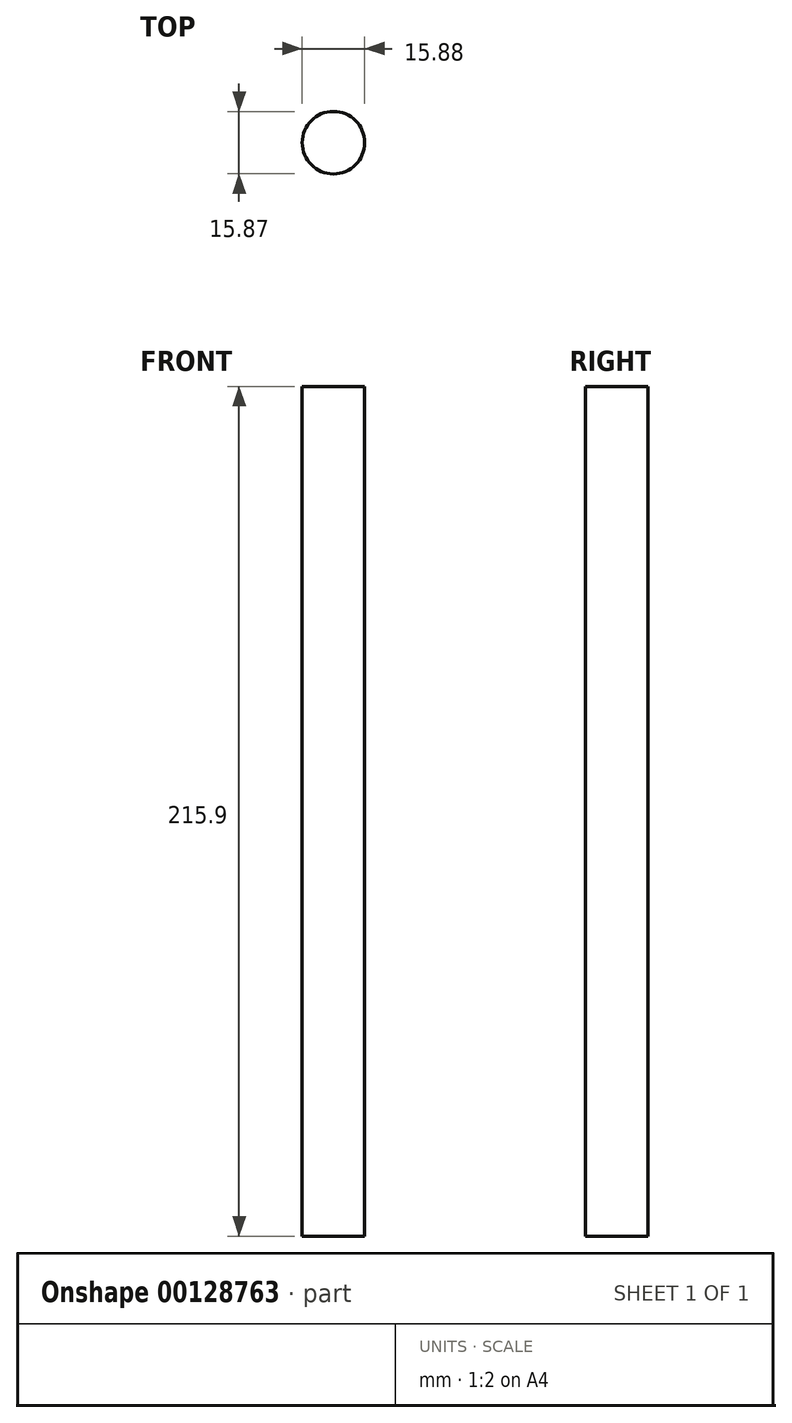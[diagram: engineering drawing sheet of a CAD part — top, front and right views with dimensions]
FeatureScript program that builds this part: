
annotation { "Feature Type Name" : "Feature", "Feature Type Description" : "" }
export const myFeature = defineFeature(function(context is Context, id is Id, definition is map)
    precondition{}
    {
        {
            var Q0;
            Q0=qCreatedBy(makeId("Top.planeOp"),FACE);
            var sketch = newSketch(context, id + "F0", { "sketchPlane" : qUnion([Q0])});
            skCircle(sketch, "E0", {"center": v(0, 0.61) * mm, "radius": 7.94 * mm});
            skSolve(sketch);
        }
        {
            var Q0;
            Q0=makeQuery(id+"F0.imprint","IMPRINT",FACE,{"disambiguationData":[TD([[makeQuery(id+"F0.imprint","IMPRINT",EDGE,{"derivedFrom":sQuery(id+"F0.wireOp",EDGE,"E0")}),1.0]])]});
            extrude(context, id + "F1", {"entities" : qUnion([Q0]), "depth" : 215.9 * mm});
        }
    });
